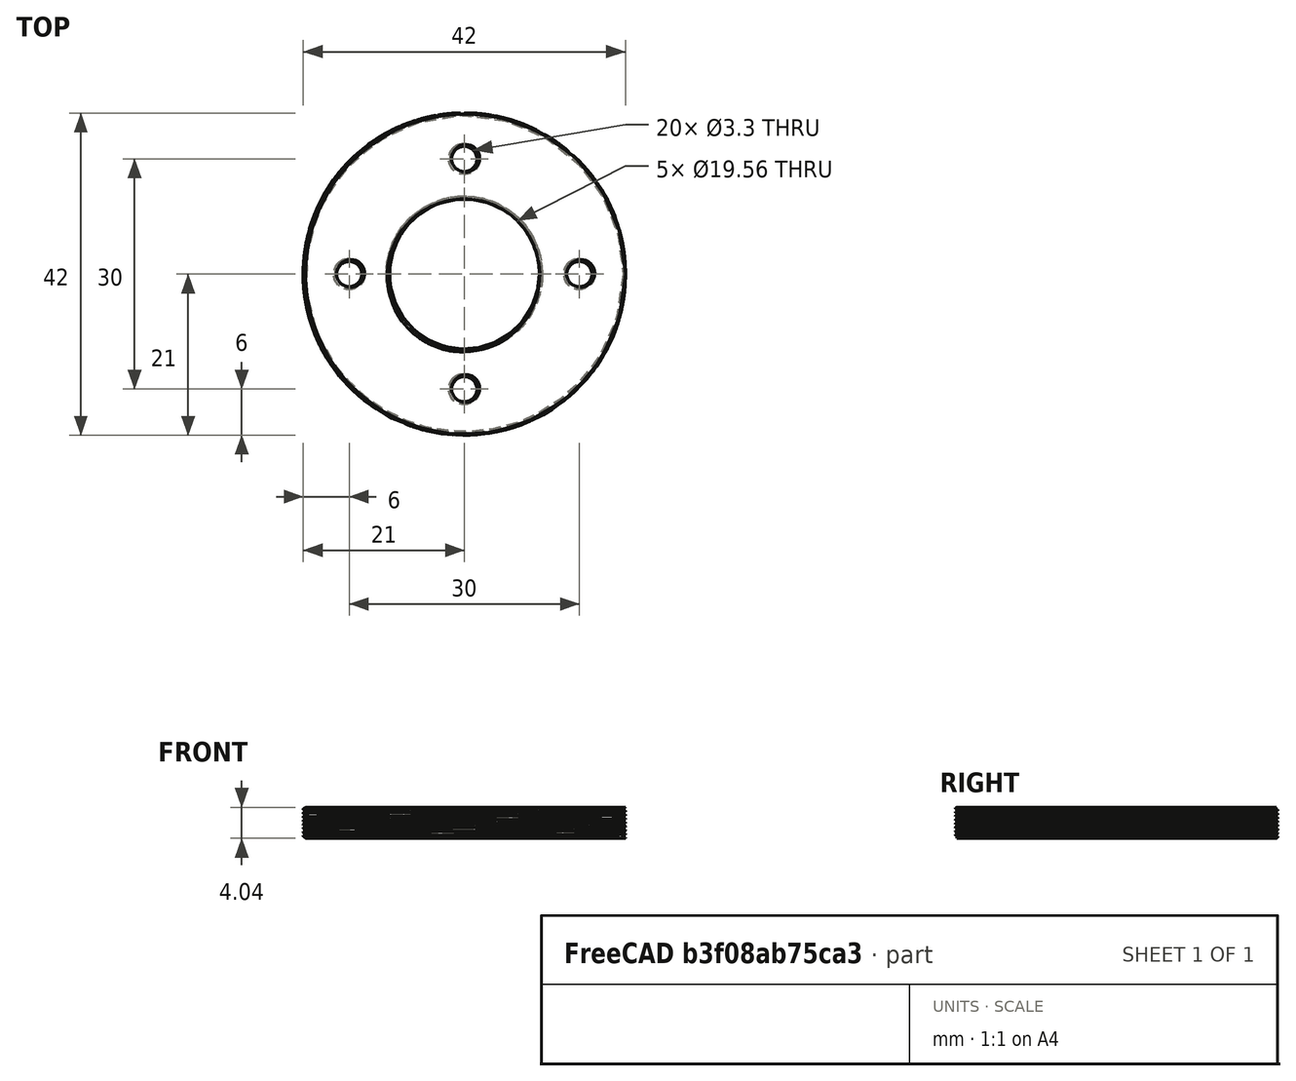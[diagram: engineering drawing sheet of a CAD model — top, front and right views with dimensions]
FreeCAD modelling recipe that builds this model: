
FCSTD DOCUMENT  (FreeCAD 0.22R0.21.2)
Label: RMS_to_M42x05_withM4Mounts
License: All rights reserved
LicenseURL: http://en.wikipedia.org/wiki/All_rights_reserved
objects: Part::Cylinder×6, Part::FeaturePython×6, Part::Cut×3, Part::MultiFuse×2, Part::Feature×1
note: 18 computed .brp shape members not serialized (recipe doc carries the construction recipe); baked Part::Feature solids carry a one-line shape summary decoded from their .brp

FEATURE [Part::Cylinder] Cylinder
  Angle = 360
  AttacherType = Attacher::AttachEngine3D
  FirstAngle = 0
  Height = 4
  Radius = 21
  SecondAngle = 0
FEATURE [Part::Cylinder] Cylinder001
  Angle = 360
  AttacherType = Attacher::AttachEngine3D
  FirstAngle = 0
  Height = 10
  Radius = 9.708
  SecondAngle = 0
FEATURE [Part::Cut] Cut
  Base = -> Cylinder
  Tool = -> Cylinder001
FEATURE [Part::Cylinder] Cylinder004
  Angle = 360
  AttacherType = Attacher::AttachEngine3D
  FirstAngle = 0
  Height = 10
  Placement = pos=(15,0,0) rot=(0,0,1;0rad)
  Radius = 1.65
  SecondAngle = 0
FEATURE [Part::FeaturePython] ScrewTap  label="20.32x8-ScrewTap_RMS"  # WARN: FeaturePython — macro-defined, semantics opaque (R4)
  Diameter = 33
  DiameterCustom = 20.32
  Invert = false
  LeftHanded = false
  Length = 8
  MatchOuter = false
  PitchCustom = 0.705612
  Placement = pos=(0,0,6) rot=(0,0,1;0rad)
  Thread = true
  Type = 3
FEATURE [Part::FeaturePython] ScrewDie  label="42x8-ScrewDie_M42x0_5"  # WARN: FeaturePython — macro-defined, semantics opaque (R4)
  Diameter = 29
  DiameterCustom = 42
  Invert = false
  LeftHanded = false
  Length = 8
  MatchOuter = false
  PitchCustom = 0.5
  Placement = pos=(0,0,6) rot=(0,0,1;0rad)
  Thread = true
  Type = 0
FEATURE [Part::Cylinder] Cylinder005
  Angle = 360
  AttacherType = Attacher::AttachEngine3D
  FirstAngle = 0
  Height = 10
  Placement = pos=(-15,0,0) rot=(0,0,1;0rad)
  Radius = 1.65
  SecondAngle = 0
FEATURE [Part::Cylinder] Cylinder006
  Angle = 360
  AttacherType = Attacher::AttachEngine3D
  FirstAngle = 0
  Height = 10
  Placement = pos=(0,15,0) rot=(0,0,1;0rad)
  Radius = 1.65
  SecondAngle = 0
FEATURE [Part::Cylinder] Cylinder007
  Angle = 360
  AttacherType = Attacher::AttachEngine3D
  FirstAngle = 0
  Height = 10
  Placement = pos=(0,-15,0) rot=(0,0,1;0rad)
  Radius = 1.65
  SecondAngle = 0
FEATURE [Part::MultiFuse] Fusion
  Shapes = -> [Cylinder007,Cylinder005,Cylinder006,Cylinder004]
FEATURE [Part::Cut] Cut001
  Base = -> Cut
  Tool = -> Fusion
FEATURE [Part::FeaturePython] ScrewTap001  label="M4x20-ScrewTap"  # WARN: FeaturePython — macro-defined, semantics opaque (R4)
  Diameter = 6
  DiameterCustom = 6
  Invert = false
  LeftHanded = false
  Length = 20
  MatchOuter = false
  PitchCustom = 1
  Placement = pos=(15,0,5) rot=(0,0,1;0rad)
  Thread = true
  Type = 2
FEATURE [Part::FeaturePython] ScrewTap002  label="M4x20-ScrewTap004"  # WARN: FeaturePython — macro-defined, semantics opaque (R4)
  Diameter = 6
  DiameterCustom = 6
  Invert = false
  LeftHanded = false
  Length = 20
  MatchOuter = false
  PitchCustom = 1
  Placement = pos=(-15,0,5) rot=(0,0,1;0rad)
  Thread = true
  Type = 2
FEATURE [Part::FeaturePython] ScrewTap003  label="M4x20-ScrewTap005"  # WARN: FeaturePython — macro-defined, semantics opaque (R4)
  Diameter = 6
  DiameterCustom = 6
  Invert = false
  LeftHanded = false
  Length = 20
  MatchOuter = false
  PitchCustom = 1
  Placement = pos=(0,15,5) rot=(0,0,1;0rad)
  Thread = true
  Type = 2
FEATURE [Part::FeaturePython] ScrewTap004  label="M4x20-ScrewTap006"  # WARN: FeaturePython — macro-defined, semantics opaque (R4)
  Diameter = 6
  DiameterCustom = 6
  Invert = false
  LeftHanded = false
  Length = 20
  MatchOuter = false
  PitchCustom = 1
  Placement = pos=(0,-15,5) rot=(0,0,1;0rad)
  Thread = true
  Type = 2
FEATURE [Part::MultiFuse] Fusion001
  Shapes = -> [ScrewTap001,ScrewTap002,ScrewTap003,ScrewTap004,ScrewDie,ScrewTap]
FEATURE [Part::Cut] Cut002  label="RMStoM42x0_5_withM4Mounts"
  Base = -> Cut001
  Tool = -> Fusion001
FEATURE [Part::Feature] Cut002_solid  label="RMStoM42x0_5_withM4Mounts (Solid)"
  shape: bbox 54.87 x 61.55 x 5.73 mm, 179 faces (baked)
